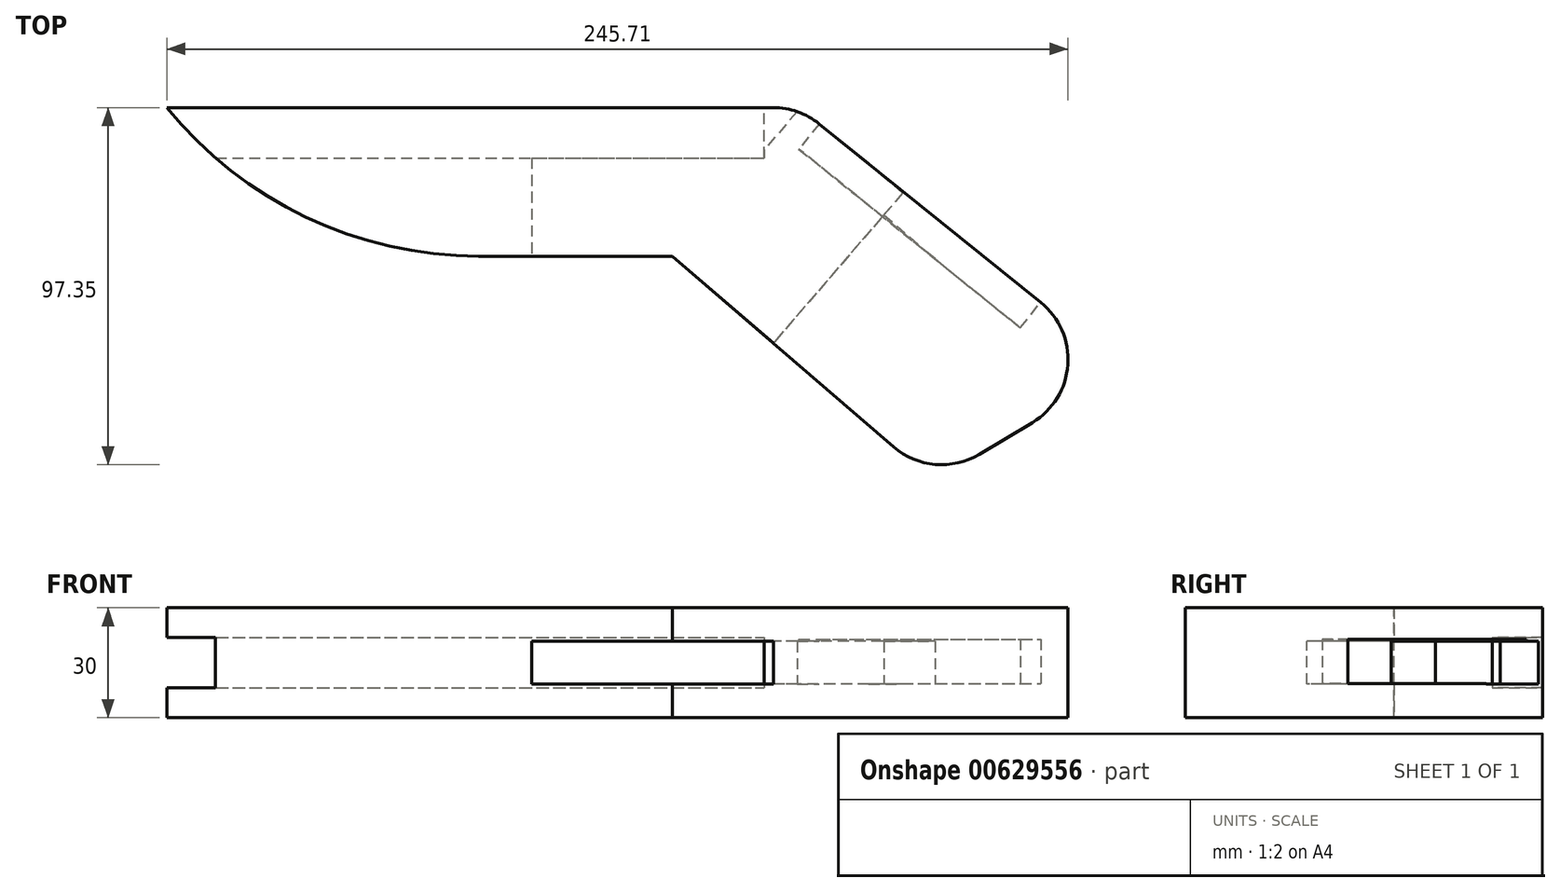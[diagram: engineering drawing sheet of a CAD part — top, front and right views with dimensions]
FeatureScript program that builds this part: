
annotation { "Feature Type Name" : "Feature", "Feature Type Description" : "" }
export const myFeature = defineFeature(function(context is Context, id is Id, definition is map)
    precondition{}
    {
        {
            var Q0;
            Q0=qCreatedBy(makeId("Top.planeOp"),FACE);
            var sketch = newSketch(context, id + "F0", { "sketchPlane" : qUnion([Q0])});
            skLineSegment(sketch, "E0", {"start": v(122.72, -164.72) * mm, "end": v(71.25, -195.55) * mm});
            skLineSegment(sketch, "E1", {"start": v(71.25, -195.55) * mm, "end": v(0, -134.12) * mm});
            skLineSegment(sketch, "E2", {"start": v(0, -134.12) * mm, "end": v(-137.86, -134.12) * mm});
            skLineSegment(sketch, "E3", {"start": v(-137.86, -134.12) * mm, "end": v(-137.86, -93.62) * mm});
            skLineSegment(sketch, "E4", {"start": v(-137.86, -93.62) * mm, "end": v(0, -93.62) * mm});
            skLineSegment(sketch, "E5", {"start": v(0, -93.62) * mm, "end": v(0, -93.62) * mm});
            skLineSegment(sketch, "E6", {"start": v(0, -93.62) * mm, "end": v(34.52, -93.62) * mm});
            skLineSegment(sketch, "E7", {"start": v(34.52, -93.62) * mm, "end": v(122.72, -164.72) * mm});
            skSolve(sketch);
        }
        {
            var Q0;
            Q0=makeQuery(id+"F0.imprint","IMPRINT",FACE,{"disambiguationData":[TD([[makeQuery(id+"F0.imprint","IMPRINT",EDGE,{"derivedFrom":sQuery(id+"F0.wireOp",EDGE,"E0")}),-1.0]])]});
            extrude(context, id + "F1", {"entities" : qUnion([Q0]), "depth" : 30 * mm, "offsetDistance" : 25 * mm});
        }
        {
            var Q0;
            Q0=makeQuery(id+"F1.opExtrude","SWEPT_EDGE",EDGE,{"disambiguationData":[OSD([sQuery(id+"F0.wireOp",EDGE,"E0"),sQuery(id+"F0.wireOp",EDGE,"E7")])]});
            var Q1;
            Q1=makeQuery(id+"F1.opExtrude","SWEPT_EDGE",EDGE,{"disambiguationData":[OSD([sQuery(id+"F0.wireOp",EDGE,"E0"),sQuery(id+"F0.wireOp",EDGE,"E1")])]});
            var Q2;
            Q2=makeQuery(id+"F1.opExtrude","SWEPT_EDGE",EDGE,{"disambiguationData":[OSD([sQuery(id+"F0.wireOp",EDGE,"E6"),sQuery(id+"F0.wireOp",EDGE,"E7")])]});
            fillet(context, id + "F2", {"entities" : qUnion([Q0, Q1, Q2]), "radius" : 20 * mm, "tangentPropagation" : true, "allowEdgeOverflow" : false});
        }
        {
            var Q0;
            Q0=makeQuery(id+"F1.opExtrude","SWEPT_FACE",FACE,{"disambiguationData":[OSD([sQuery(id+"F0.wireOp",EDGE,"E4"),sQuery(id+"F0.wireOp",EDGE,"E6")])]});
            var sketch = newSketch(context, id + "F3", { "sketchPlane" : qUnion([Q0])});
            skSolve(sketch);
        }
        {
            var Q0;
            Q0=makeQuery(id+"F1.opExtrude","SWEPT_FACE",FACE,{"disambiguationData":[OSD([sQuery(id+"F0.wireOp",EDGE,"E7")])]});
            var sketch = newSketch(context, id + "F4", { "sketchPlane" : qUnion([Q0])});
            skLineSegment(sketch, "E8.bottom", {"start": v(-92.68, 21.42) * mm, "end": v(-170.25, 21.42) * mm});
            skLineSegment(sketch, "E8.top", {"start": v(-92.68, 9.32) * mm, "end": v(-170.25, 9.32) * mm});
            skLineSegment(sketch, "E8.left", {"start": v(-92.68, 21.42) * mm, "end": v(-92.68, 9.32) * mm});
            skLineSegment(sketch, "E8.right", {"start": v(-170.25, 21.42) * mm, "end": v(-170.25, 9.32) * mm});
            skSolve(sketch);
        }
        {
            var Q0;
            Q0 = qSketchRegion(id + "F4", true);
            extrude(context, id + "F5", {"entities" : qUnion([Q0]), "operationType" : NewBodyOperationType.REMOVE, "oppositeDirection" : true, "depth" : 8.85 * mm, "offsetDistance" : 25 * mm});
        }
        {
            var Q0;
            {var subQ0=sQuery(id+"F0.wireOp",EDGE,"E4");Q0=makeQuery(id+"F3.imprint","IMPRINT",FACE,{"disambiguationData":[TD([[makeQuery(id+"F3.imprint","IMPRINT",EDGE,{"derivedFrom":makeQuery(id+"F1.opExtrude","SWEPT_EDGE",EDGE,{"disambiguationData":[OSD([sQuery(id+"F0.wireOp",EDGE,"E3"),subQ0])]})}),-1.0]])]});}
            var sketch = newSketch(context, id + "F6", { "sketchPlane" : qUnion([Q0])});
            skLineSegment(sketch, "E9.bottom", {"start": v(138.3, 21.92) * mm, "end": v(0, 21.92) * mm});
            skLineSegment(sketch, "E9.top", {"start": v(138.3, 8.21) * mm, "end": v(0, 8.21) * mm});
            skLineSegment(sketch, "E9.left", {"start": v(138.3, 21.92) * mm, "end": v(138.3, 8.21) * mm});
            skLineSegment(sketch, "E9.right", {"start": v(0, 21.92) * mm, "end": v(0, 8.21) * mm});
            skSolve(sketch);
        }
        {
            var Q0;
            Q0 = qSketchRegion(id + "F6", true);
            extrude(context, id + "F7", {"entities" : qUnion([Q0]), "operationType" : NewBodyOperationType.REMOVE, "oppositeDirection" : true, "depth" : 13.75 * mm, "offsetDistance" : 25 * mm});
        }
        {
            var Q0;
            Q0=makeQuery(id+"F1.opExtrude","SWEPT_EDGE",EDGE,{"disambiguationData":[OSD([sQuery(id+"F0.wireOp",EDGE,"E2"),sQuery(id+"F0.wireOp",EDGE,"E3")])]});
            fillet(context, id + "F8", {"entities" : qUnion([Q0]), "radius" : 109.5 * mm, "tangentPropagation" : true, "allowEdgeOverflow" : false});
        }
        {
            var Q0;
            Q0=makeQuery(id+"F1.opExtrude","SWEPT_FACE",FACE,{"disambiguationData":[OSD([sQuery(id+"F0.wireOp",EDGE,"E2")])]});
            var sketch = newSketch(context, id + "F9", { "sketchPlane" : qUnion([Q0])});
            skLineSegment(sketch, "E10.bottom", {"start": v(0, 9.17) * mm, "end": v(-38.42, 9.17) * mm});
            skLineSegment(sketch, "E10.top", {"start": v(0, 20.83) * mm, "end": v(-38.42, 20.83) * mm});
            skLineSegment(sketch, "E10.left", {"start": v(0, 9.17) * mm, "end": v(0, 20.83) * mm});
            skLineSegment(sketch, "E10.right", {"start": v(-38.42, 9.17) * mm, "end": v(-38.42, 20.83) * mm});
            skPoint(sketch, "E10.middle", {"position": v(-19.2, 15) * mm});
            skPoint(sketch, "E10.middle.positionSnap0", {"position": v(0, 15) * mm});
            skPoint(sketch, "E10.centerSnap0", {"position": v(0, 15) * mm});
            skSolve(sketch);
        }
        {
            var Q0;
            Q0 = qSketchRegion(id + "F9", true);
            extrude(context, id + "F10", {"entities" : qUnion([Q0]), "operationType" : NewBodyOperationType.REMOVE, "oppositeDirection" : true, "depth" : 41.76 * mm, "offsetDistance" : 25 * mm});
        }
        {
            var Q0;
            Q0=makeQuery(id+"F1.opExtrude","SWEPT_FACE",FACE,{"disambiguationData":[OSD([sQuery(id+"F0.wireOp",EDGE,"E1")])]});
            var sketch = newSketch(context, id + "F11", { "sketchPlane" : qUnion([Q0])});
            skLineSegment(sketch, "E11.bottom", {"start": v(87.58, 9.17) * mm, "end": v(142.26, 9.17) * mm});
            skLineSegment(sketch, "E11.top", {"start": v(87.58, 20.83) * mm, "end": v(142.26, 20.83) * mm});
            skLineSegment(sketch, "E11.left", {"start": v(87.58, 9.17) * mm, "end": v(87.58, 20.83) * mm});
            skLineSegment(sketch, "E11.right", {"start": v(142.26, 9.17) * mm, "end": v(142.26, 20.83) * mm});
            skSolve(sketch);
        }
        {
            var Q0;
            Q0 = qSketchRegion(id + "F11", true);
            var Q1;
            Q1=makeQuery(id+"F11.imprint","IMPRINT",FACE,{"disambiguationData":[TD([[makeQuery(id+"F11.imprint","IMPRINT",EDGE,{"derivedFrom":sQuery(id+"F11.wireOp",EDGE,"E11.bottom")}),1.0]])]});
            extrude(context, id + "F12", {"entities" : qUnion([Q0, Q1]), "operationType" : NewBodyOperationType.REMOVE, "oppositeDirection" : true, "depth" : 54.02 * mm, "offsetDistance" : 25 * mm});
        }
        {
            var Q0;
            Q0=makeQuery(id+"F10.boolean.opBoolean","MERGE",FACE,{"derivedFrom":[makeQuery(id+"F7.boolean.opBoolean","COPY",FACE,{"derivedFrom":makeQuery(id+"F7.opExtrude","SWEPT_FACE",FACE,{"disambiguationData":[OSD([sQuery(id+"F6.wireOp",EDGE,"E9.right")])]})}),makeQuery(id+"F10.opExtrude","SWEPT_FACE",FACE,{"disambiguationData":[OSD([sQuery(id+"F9.wireOp",EDGE,"E10.left")])]})]});
            extrude(context, id + "F13", {"entities" : qUnion([Q0]), "operationType" : NewBodyOperationType.REMOVE, "oppositeDirection" : true, "depth" : 25 * mm, "offsetDistance" : 25 * mm});
        }
        {
            var Q0;
            Q0=makeQuery(id+"F12.boolean.opBoolean","COPY",FACE,{"derivedFrom":makeQuery(id+"F12.opExtrude","SWEPT_FACE",FACE,{"disambiguationData":[OSD([sQuery(id+"F11.wireOp",EDGE,"E11.right")])]})});
            extrude(context, id + "F14", {"entities" : qUnion([Q0]), "operationType" : NewBodyOperationType.ADD, "depth" : 18.36 * mm, "offsetDistance" : 25 * mm});
        }
        {
            var Q0;
            Q0=makeQuery(id+"F10.boolean.opBoolean","COPY",FACE,{"derivedFrom":makeQuery(id+"F10.opExtrude","SWEPT_FACE",FACE,{"disambiguationData":[OSD([sQuery(id+"F9.wireOp",EDGE,"E10.right")])]})});
            extrude(context, id + "F15", {"entities" : qUnion([Q0]), "operationType" : NewBodyOperationType.REMOVE, "depth" : 10.4 * mm, "offsetDistance" : 25 * mm});
        }
    });
